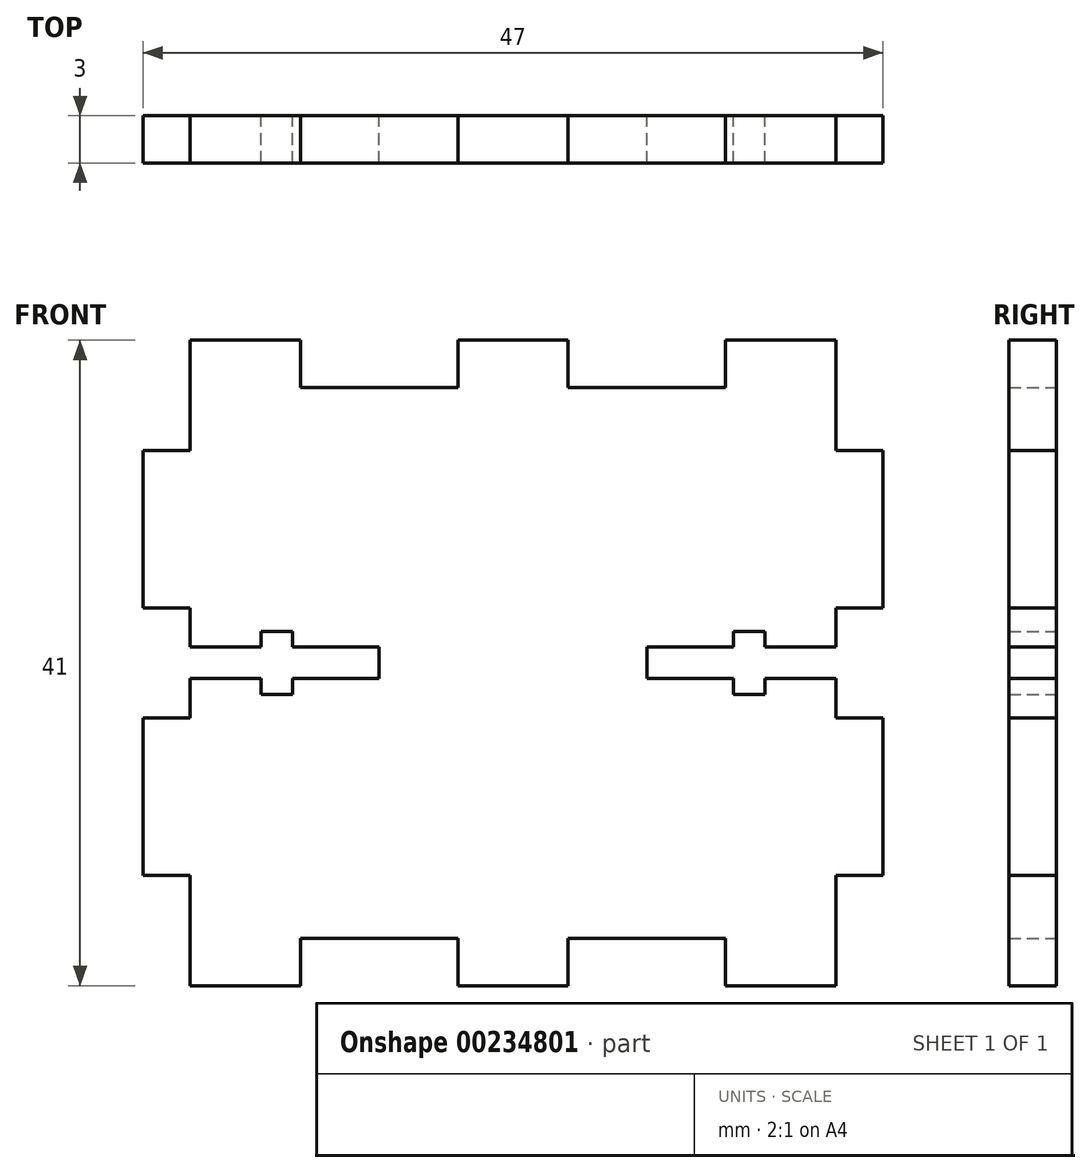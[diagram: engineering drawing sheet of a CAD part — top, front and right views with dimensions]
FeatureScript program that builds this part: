
annotation { "Feature Type Name" : "Feature", "Feature Type Description" : "" }
export const myFeature = defineFeature(function(context is Context, id is Id, definition is map)
    precondition{}
    {
        {
            var Q0;
            Q0=qCreatedBy(makeId("Front.planeOp"),FACE);
            var sketch = newSketch(context, id + "F0", { "sketchPlane" : qUnion([Q0])});
            skLineSegment(sketch, "E0.bottom", {"start": v(0, 0) * mm, "end": v(8.5, 0) * mm});
            skLineSegment(sketch, "E0.top", {"start": v(3.5, 17.5) * mm, "end": v(13.5, 17.5) * mm});
            skLineSegment(sketch, "E0.left", {"start": v(0, 0) * mm, "end": v(0, 17.5) * mm});
            skLineSegment(sketch, "E0.right", {"start": v(20.5, 1) * mm, "end": v(20.5, 17.5) * mm});
            skLineSegment(sketch, "E1", {"start": v(20.5, 17.5) * mm, "end": v(20.5, 20.5) * mm});
            skLineSegment(sketch, "E2", {"start": v(20.5, 20.5) * mm, "end": v(13.5, 20.5) * mm});
            skLineSegment(sketch, "E3", {"start": v(13.5, 20.5) * mm, "end": v(13.5, 17.5) * mm});
            skLineSegment(sketch, "E4", {"start": v(0, 17.5) * mm, "end": v(0, 20.5) * mm});
            skPoint(sketch, "E4.endSnap0", {"position": v(17, 20.5) * mm});
            skLineSegment(sketch, "E5", {"start": v(0, 20.5) * mm, "end": v(3.5, 20.5) * mm});
            skLineSegment(sketch, "E6", {"start": v(3.5, 20.5) * mm, "end": v(3.5, 17.5) * mm});
            skLineSegment(sketch, "E7", {"start": v(20.5, 13.5) * mm, "end": v(23.5, 13.5) * mm});
            skLineSegment(sketch, "E8", {"start": v(23.5, 13.5) * mm, "end": v(23.5, 3.5) * mm});
            skLineSegment(sketch, "E9", {"start": v(23.5, 3.5) * mm, "end": v(20.5, 3.5) * mm});
            skLineSegment(sketch, "E10", {"start": v(20.5, 1) * mm, "end": v(16, 1) * mm});
            skLineSegment(sketch, "E11", {"start": v(8.5, 1) * mm, "end": v(8.5, 0) * mm});
            skLineSegment(sketch, "E12", {"start": v(14, 1) * mm, "end": v(14, 2) * mm});
            skLineSegment(sketch, "E13", {"start": v(16, 2) * mm, "end": v(14, 2) * mm});
            skLineSegment(sketch, "E14", {"start": v(16, 2) * mm, "end": v(16, 1) * mm});
            skLineSegment(sketch, "E15.trimOffspring", {"start": v(14, 1) * mm, "end": v(8.5, 1) * mm});
            skLineSegment(sketch, "E16.MirrorCS", {"start": v(16, -2) * mm, "end": v(16, -1) * mm});
            skLineSegment(sketch, "E17.MirrorCS", {"start": v(8.5, -1) * mm, "end": v(8.5, 0) * mm});
            skLineSegment(sketch, "E18.MirrorCS", {"start": v(14, -1) * mm, "end": v(14, -2) * mm});
            skLineSegment(sketch, "E19.MirrorCS", {"start": v(16, -2) * mm, "end": v(14, -2) * mm});
            skLineSegment(sketch, "E20.MirrorCS", {"start": v(14, -1) * mm, "end": v(8.5, -1) * mm});
            skLineSegment(sketch, "E21.MirrorCS", {"start": v(23.5, -3.5) * mm, "end": v(20.5, -3.5) * mm});
            skLineSegment(sketch, "E22.MirrorCS", {"start": v(23.5, -13.5) * mm, "end": v(23.5, -3.5) * mm});
            skLineSegment(sketch, "E23.MirrorCS", {"start": v(20.5, -13.5) * mm, "end": v(23.5, -13.5) * mm});
            skLineSegment(sketch, "E24.MirrorCS", {"start": v(13.5, -20.5) * mm, "end": v(13.5, -17.5) * mm});
            skLineSegment(sketch, "E25.MirrorCS", {"start": v(0, -17.5) * mm, "end": v(0, -20.5) * mm});
            skLineSegment(sketch, "E26.MirrorCS", {"start": v(20.5, -20.5) * mm, "end": v(13.5, -20.5) * mm});
            skLineSegment(sketch, "E27.MirrorCS", {"start": v(0, -20.5) * mm, "end": v(3.5, -20.5) * mm});
            skLineSegment(sketch, "E28.MirrorCS", {"start": v(3.5, -20.5) * mm, "end": v(3.5, -17.5) * mm});
            skLineSegment(sketch, "E29.MirrorCS", {"start": v(20.5, -1) * mm, "end": v(16, -1) * mm});
            skLineSegment(sketch, "E30.MirrorCS", {"start": v(20.5, -17.5) * mm, "end": v(20.5, -20.5) * mm});
            skLineSegment(sketch, "E31.MirrorCS", {"start": v(20.5, -1) * mm, "end": v(20.5, -17.5) * mm});
            skLineSegment(sketch, "E32.MirrorCS", {"start": v(0, 0) * mm, "end": v(0, -17.5) * mm});
            skPoint(sketch, "E33.MirrorP", {"position": v(17, -20.5) * mm});
            skLineSegment(sketch, "E34.MirrorCS", {"start": v(3.5, -17.5) * mm, "end": v(13.5, -17.5) * mm});
            skLineSegment(sketch, "E35.MirrorCS", {"start": v(-8.5, -1) * mm, "end": v(-8.5, 0) * mm});
            skLineSegment(sketch, "E36.MirrorCS", {"start": v(-8.5, 1) * mm, "end": v(-8.5, 0) * mm});
            skLineSegment(sketch, "E37.MirrorCS", {"start": v(-14, 1) * mm, "end": v(-14, 2) * mm});
            skLineSegment(sketch, "E38.MirrorCS", {"start": v(-16, 2) * mm, "end": v(-16, 1) * mm});
            skLineSegment(sketch, "E39.MirrorCS", {"start": v(-16, 2) * mm, "end": v(-14, 2) * mm});
            skLineSegment(sketch, "E40.MirrorCS", {"start": v(-16, -2) * mm, "end": v(-16, -1) * mm});
            skLineSegment(sketch, "E41.MirrorCS", {"start": v(-16, -2) * mm, "end": v(-14, -2) * mm});
            skLineSegment(sketch, "E42.MirrorCS", {"start": v(-14, -1) * mm, "end": v(-14, -2) * mm});
            skLineSegment(sketch, "E43.MirrorCS", {"start": v(-13.5, -20.5) * mm, "end": v(-13.5, -17.5) * mm});
            skLineSegment(sketch, "E44.MirrorCS", {"start": v(-20.5, -17.5) * mm, "end": v(-20.5, -20.5) * mm});
            skLineSegment(sketch, "E45.MirrorCS", {"start": v(-3.5, 20.5) * mm, "end": v(-3.5, 17.5) * mm});
            skLineSegment(sketch, "E46.MirrorCS", {"start": v(-3.5, -20.5) * mm, "end": v(-3.5, -17.5) * mm});
            skLineSegment(sketch, "E47.MirrorCS", {"start": v(-13.5, 20.5) * mm, "end": v(-13.5, 17.5) * mm});
            skLineSegment(sketch, "E48.MirrorCS", {"start": v(-20.5, 17.5) * mm, "end": v(-20.5, 20.5) * mm});
            skLineSegment(sketch, "E49.MirrorCS", {"start": v(-20.5, -20.5) * mm, "end": v(-13.5, -20.5) * mm});
            skLineSegment(sketch, "E50.MirrorCS", {"start": v(0, 0) * mm, "end": v(-8.5, 0) * mm});
            skLineSegment(sketch, "E51.MirrorCS", {"start": v(-20.5, 20.5) * mm, "end": v(-13.5, 20.5) * mm});
            skLineSegment(sketch, "E52.MirrorCS", {"start": v(-20.5, 1) * mm, "end": v(-16, 1) * mm});
            skLineSegment(sketch, "E53.MirrorCS", {"start": v(-23.5, 3.5) * mm, "end": v(-20.5, 3.5) * mm});
            skLineSegment(sketch, "E54.MirrorCS", {"start": v(-20.5, -13.5) * mm, "end": v(-23.5, -13.5) * mm});
            skLineSegment(sketch, "E55.MirrorCS", {"start": v(-3.5, 17.5) * mm, "end": v(-13.5, 17.5) * mm});
            skLineSegment(sketch, "E56.MirrorCS", {"start": v(-20.5, -1) * mm, "end": v(-20.5, -17.5) * mm});
            skLineSegment(sketch, "E57.MirrorCS", {"start": v(-14, -1) * mm, "end": v(-8.5, -1) * mm});
            skLineSegment(sketch, "E58.MirrorCS", {"start": v(0, -20.5) * mm, "end": v(-3.5, -20.5) * mm});
            skPoint(sketch, "E59.MirrorP", {"position": v(-17, 20.5) * mm});
            skLineSegment(sketch, "E60.MirrorCS", {"start": v(-23.5, -3.5) * mm, "end": v(-20.5, -3.5) * mm});
            skLineSegment(sketch, "E61.MirrorCS", {"start": v(-23.5, 13.5) * mm, "end": v(-23.5, 3.5) * mm});
            skLineSegment(sketch, "E62.MirrorCS", {"start": v(-23.5, -13.5) * mm, "end": v(-23.5, -3.5) * mm});
            skLineSegment(sketch, "E63.MirrorCS", {"start": v(-3.5, -17.5) * mm, "end": v(-13.5, -17.5) * mm});
            skPoint(sketch, "E64.MirrorP", {"position": v(-17, -20.5) * mm});
            skLineSegment(sketch, "E65.MirrorCS", {"start": v(0, 20.5) * mm, "end": v(-3.5, 20.5) * mm});
            skLineSegment(sketch, "E66.MirrorCS", {"start": v(-20.5, 1) * mm, "end": v(-20.5, 17.5) * mm});
            skLineSegment(sketch, "E67.MirrorCS", {"start": v(-14, 1) * mm, "end": v(-8.5, 1) * mm});
            skLineSegment(sketch, "E68.MirrorCS", {"start": v(-20.5, -1) * mm, "end": v(-16, -1) * mm});
            skLineSegment(sketch, "E69.MirrorCS", {"start": v(-20.5, 13.5) * mm, "end": v(-23.5, 13.5) * mm});
            skSolve(sketch);
        }
        {
            var Q0;
            Q0 = qSketchRegion(id + "F0", true);
            extrude(context, id + "F1", {"entities" : qUnion([Q0]), "endBound" : BoundingType.SYMMETRIC, "depth" : 3 * mm});
        }
    });
